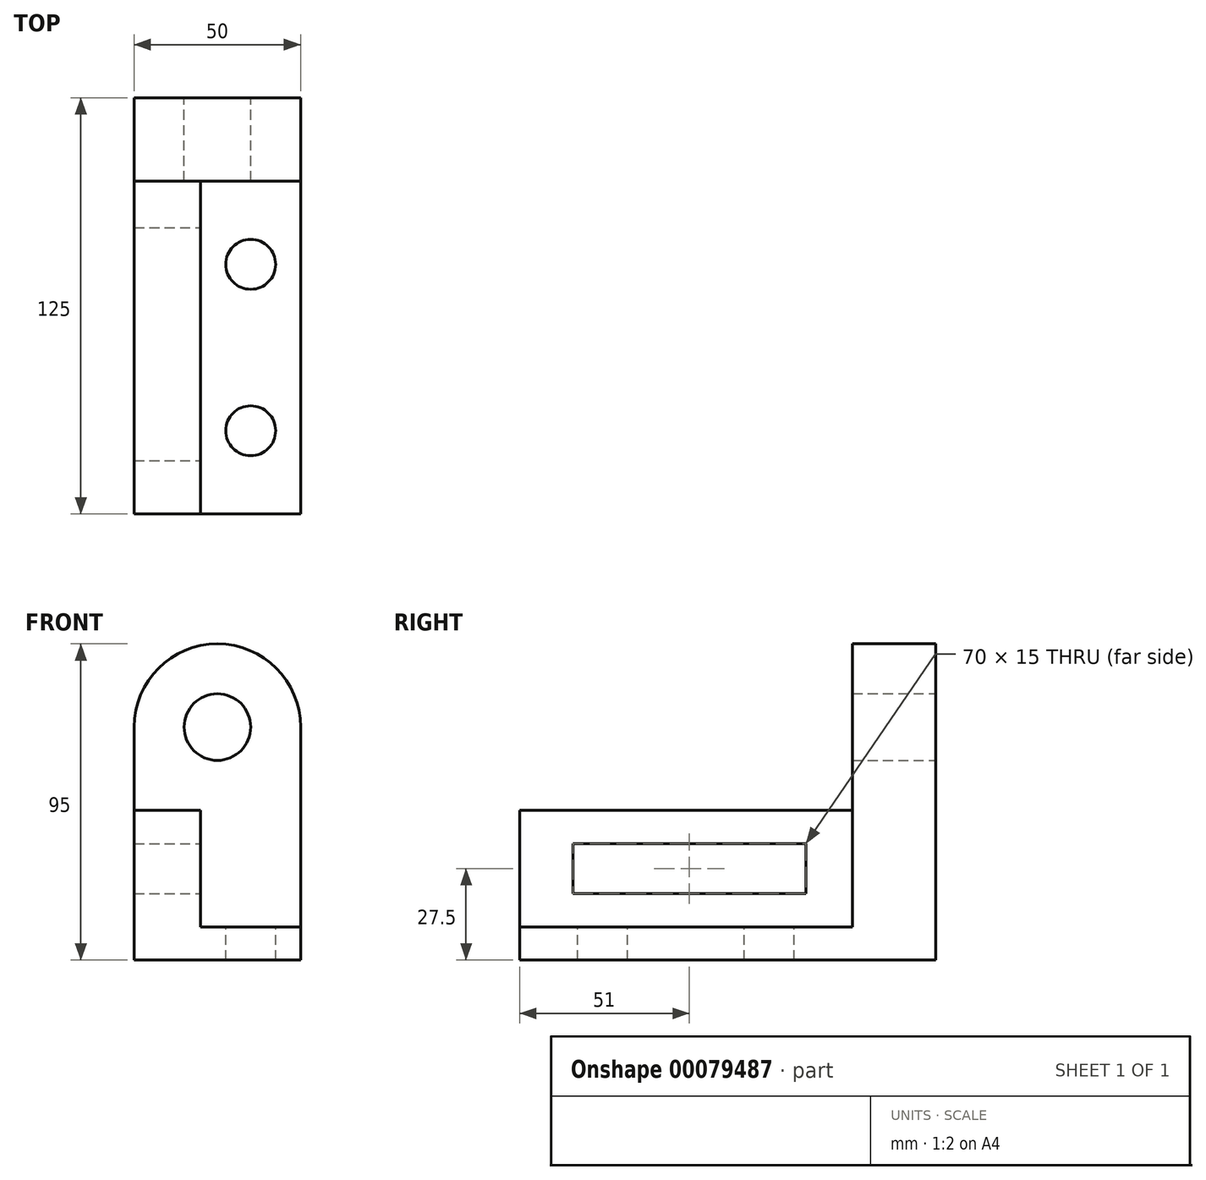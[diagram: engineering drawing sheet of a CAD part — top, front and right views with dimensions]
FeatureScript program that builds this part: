
annotation { "Feature Type Name" : "Feature", "Feature Type Description" : "" }
export const myFeature = defineFeature(function(context is Context, id is Id, definition is map)
    precondition{}
    {
        {
            var Q0;
            Q0=qCreatedBy(makeId("Front.planeOp"),FACE);
            var sketch = newSketch(context, id + "F0", { "sketchPlane" : qUnion([Q0])});
            skLineSegment(sketch, "E0", {"start": v(0, 45) * mm, "end": v(0, 0) * mm});
            skLineSegment(sketch, "E1", {"start": v(0, 45) * mm, "end": v(20, 45) * mm});
            skLineSegment(sketch, "E2", {"start": v(20, 45) * mm, "end": v(20, 10) * mm});
            skLineSegment(sketch, "E3", {"start": v(20, 10) * mm, "end": v(50, 10) * mm});
            skLineSegment(sketch, "E4", {"start": v(50, 10) * mm, "end": v(50, 0) * mm});
            skLineSegment(sketch, "E5", {"start": v(50, 0) * mm, "end": v(0, 0) * mm});
            skSolve(sketch);
        }
        {
            var Q0;
            Q0 = qSketchRegion(id + "F0", true);
            extrude(context, id + "F1", {"entities" : qUnion([Q0]), "depth" : 100 * mm});
        }
        {
            var Q0;
            Q0=makeQuery(id+"F1.opExtrude","SWEPT_FACE",FACE,{"disambiguationData":[OSD([sQuery(id+"F0.wireOp",EDGE,"E2")])]});
            var sketch = newSketch(context, id + "F2", { "sketchPlane" : qUnion([Q0])});
            skLineSegment(sketch, "E6.bottom", {"start": v(-84, 35) * mm, "end": v(-14, 35) * mm});
            skLineSegment(sketch, "E6.top", {"start": v(-84, 20) * mm, "end": v(-14, 20) * mm});
            skLineSegment(sketch, "E6.left", {"start": v(-84, 35) * mm, "end": v(-84, 20) * mm});
            skLineSegment(sketch, "E6.right", {"start": v(-14, 35) * mm, "end": v(-14, 20) * mm});
            skSolve(sketch);
        }
        {
            var Q0;
            Q0=makeQuery(id+"F2.imprint","IMPRINT",FACE,{"disambiguationData":[TD([[makeQuery(id+"F2.imprint","IMPRINT",EDGE,{"derivedFrom":sQuery(id+"F2.wireOp",EDGE,"E6.bottom")}),-1.0]])]});
            extrude(context, id + "F3", {"entities" : qUnion([Q0]), "operationType" : NewBodyOperationType.REMOVE, "oppositeDirection" : true, "depth" : 25.4 * mm});
        }
        {
            var Q0;
            Q0=qCreatedBy(makeId("Right.planeOp"),FACE);
            var sketch = newSketch(context, id + "F4", { "sketchPlane" : qUnion([Q0])});
            skLineSegment(sketch, "E7", {"start": v(0, 0) * mm, "end": v(25, 0) * mm});
            skLineSegment(sketch, "E8", {"start": v(25, 0) * mm, "end": v(25, 70) * mm});
            skLineSegment(sketch, "E9", {"start": v(25, 70) * mm, "end": v(0, 70) * mm});
            skLineSegment(sketch, "E10", {"start": v(0, 70) * mm, "end": v(0, 0) * mm});
            skSolve(sketch);
        }
        {
            var Q0;
            Q0=makeQuery(id+"F4.imprint","IMPRINT",FACE,{"disambiguationData":[TD([[makeQuery(id+"F4.imprint","IMPRINT",EDGE,{"derivedFrom":sQuery(id+"F4.wireOp",EDGE,"E7")}),1.0]])]});
            extrude(context, id + "F5", {"entities" : qUnion([Q0]), "operationType" : NewBodyOperationType.ADD, "depth" : 50 * mm});
        }
        {
            var Q0;
            Q0=makeQuery(id+"F5.opExtrude","SWEPT_FACE",FACE,{"disambiguationData":[OSD([sQuery(id+"F4.wireOp",EDGE,"E8")])]});
            var sketch = newSketch(context, id + "F6", { "sketchPlane" : qUnion([Q0])});
            skLineSegment(sketch, "E11", {"start": v(-50, 70) * mm, "end": v(0, 70) * mm});
            skArc(sketch, "E12", {"start": v(0, 70) * mm, "mid": v(-25, 95) * mm, "end": v(-50, 70) * mm});
            skSolve(sketch);
        }
        {
            var Q0;
            Q0=makeQuery(id+"F6.imprint","IMPRINT",FACE,{"disambiguationData":[TD([[makeQuery(id+"F6.imprint","IMPRINT",EDGE,{"derivedFrom":sQuery(id+"F6.wireOp",EDGE,"E11")}),1.0]])]});
            extrude(context, id + "F7", {"entities" : qUnion([Q0]), "operationType" : NewBodyOperationType.ADD, "oppositeDirection" : true, "depth" : 25 * mm});
        }
        {
            var Q0;
            Q0=makeQuery(id+"F7.boolean.opBoolean","MERGE",FACE,{"derivedFrom":[makeQuery(id+"F5.opExtrude","SWEPT_FACE",FACE,{"disambiguationData":[OSD([sQuery(id+"F4.wireOp",EDGE,"E8")])]}),makeQuery(id+"F7.opExtrude","CAP_FACE",FACE,{"disambiguationData":[OSD([sQuery(id+"F6.wireOp",EDGE,"E11"),sQuery(id+"F6.wireOp",EDGE,"E12")])],"isStart":true})]});
            var sketch = newSketch(context, id + "F8", { "sketchPlane" : qUnion([Q0])});
            skCircle(sketch, "E13", {"center": v(-25, 70) * mm, "radius": 10 * mm});
            skPoint(sketch, "E13.centerSnap0", {"position": v(-25, 95) * mm});
            skSolve(sketch);
        }
        {
            var Q0;
            Q0=makeQuery(id+"F8.imprint","IMPRINT",FACE,{"disambiguationData":[TD([[makeQuery(id+"F8.imprint","IMPRINT",EDGE,{"derivedFrom":sQuery(id+"F8.wireOp",EDGE,"E13")}),1.0]])]});
            extrude(context, id + "F9", {"entities" : qUnion([Q0]), "operationType" : NewBodyOperationType.REMOVE, "oppositeDirection" : true, "depth" : 25.4 * mm});
        }
        {
            var Q0;
            Q0=makeQuery(id+"F1.opExtrude","SWEPT_FACE",FACE,{"disambiguationData":[OSD([sQuery(id+"F0.wireOp",EDGE,"E3")])]});
            var sketch = newSketch(context, id + "F10", { "sketchPlane" : qUnion([Q0])});
            skCircle(sketch, "E14", {"center": v(35, -25) * mm, "radius": 7.5 * mm});
            skPoint(sketch, "E14.centerSnap0", {"position": v(35, 0) * mm});
            skCircle(sketch, "E15", {"center": v(35, -75) * mm, "radius": 7.5 * mm});
            skSolve(sketch);
        }
        {
            var Q0;
            Q0 = qSketchRegion(id + "F10", true);
            extrude(context, id + "F11", {"entities" : qUnion([Q0]), "operationType" : NewBodyOperationType.REMOVE, "oppositeDirection" : true, "depth" : 25.4 * mm});
        }
    });
